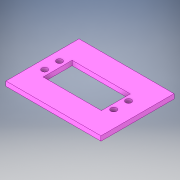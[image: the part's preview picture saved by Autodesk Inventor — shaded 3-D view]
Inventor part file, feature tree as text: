
AUTODESK INVENTOR PART (.ipt)
format: ipt  version: 2019 (Build 230136000, 136)  size: 136,192 bytes
history: native  units: mm
features: extrude x1, sketch x1
ambient origin geometry x8: Origin, YZ Plane, XZ Plane, XY Plane, X Axis, Y Axis, Z Axis, Center Point
bodies: Solid1 (feature_tree)
feature tree (2):
  extrude  "Extrusion1"  Depth=3.18mm
  sketch  "Sketch1"  dims[d0=4.0mm d1=4.0mm d2=4.0mm d3=4.0mm d4=13.47mm d5=5.085mm d6=10.17mm d7=13.47mm d8=33.79mm d9=5.085mm d10=10.17mm d12=50.0mm d13=65.0mm d15=25.0mm d25=9.66mm d26=19.82mm d27=9.91mm d28=39.88mm d29=33.79mm d30=20.0mm d31=3.18mm d32=0.0mm]
